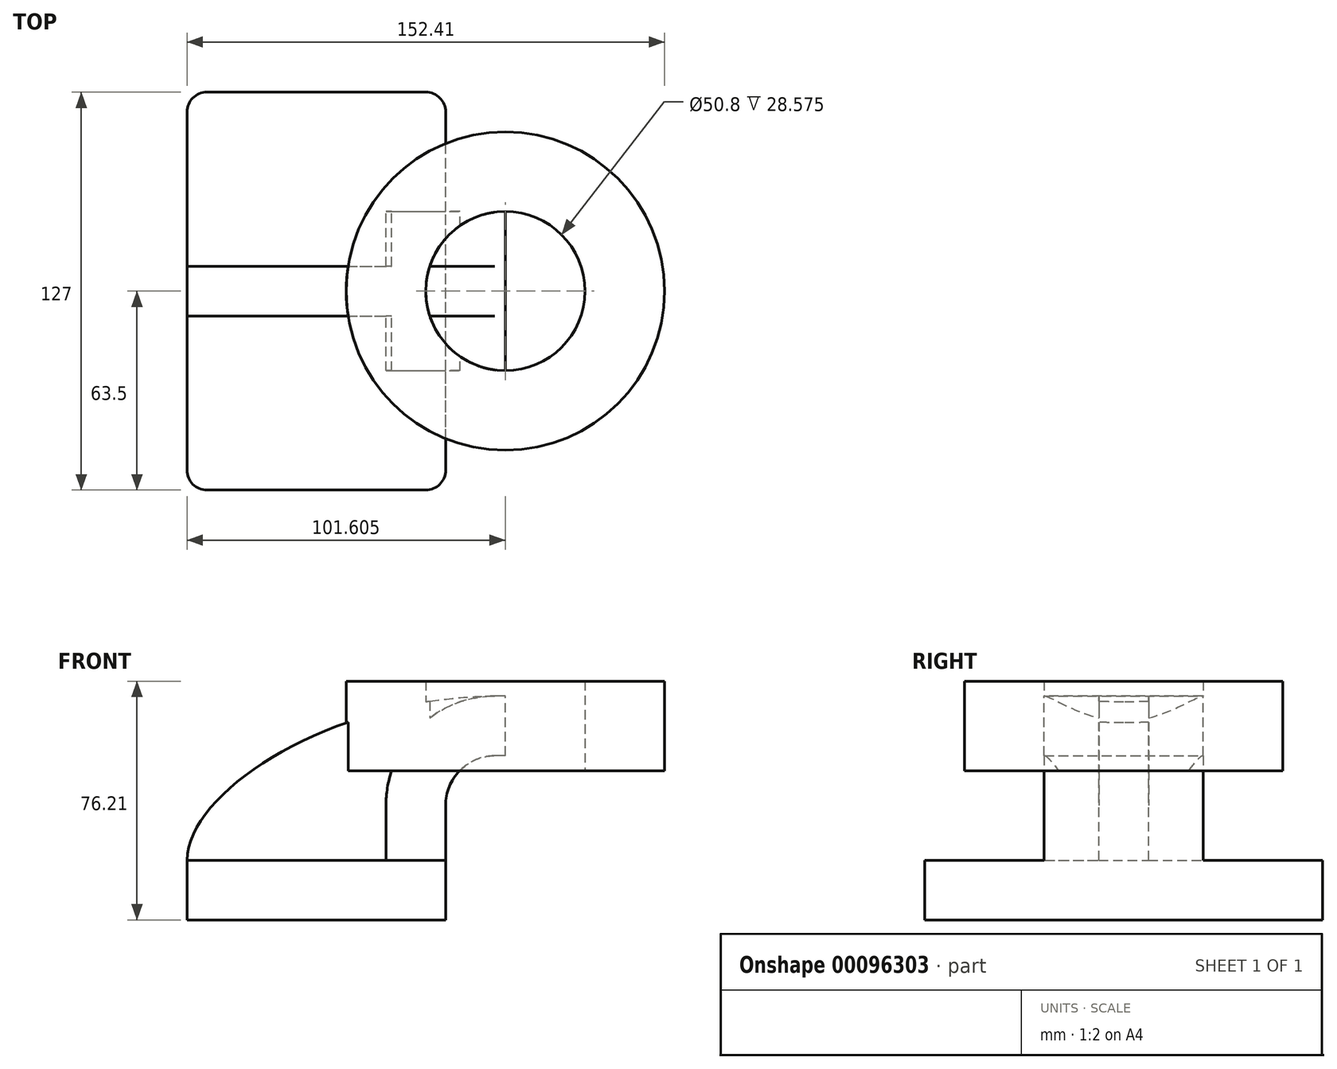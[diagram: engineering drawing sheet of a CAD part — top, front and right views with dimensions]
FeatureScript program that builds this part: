
annotation { "Feature Type Name" : "Feature", "Feature Type Description" : "" }
export const myFeature = defineFeature(function(context is Context, id is Id, definition is map)
    precondition{}
    {
        {
            var Q0;
            Q0=qCreatedBy(makeId("Front.planeOp"),FACE);
            var sketch = newSketch(context, id + "F0", { "sketchPlane" : qUnion([Q0])});
            skLineSegment(sketch, "E0.bottom", {"start": v(-41.28, -9.53) * mm, "end": v(41.28, -9.53) * mm});
            skLineSegment(sketch, "E0.top", {"start": v(-41.28, 9.53) * mm, "end": v(41.28, 9.53) * mm});
            skLineSegment(sketch, "E0.left", {"start": v(-41.28, -9.53) * mm, "end": v(-41.28, 9.53) * mm});
            skLineSegment(sketch, "E0.right", {"start": v(41.28, -9.53) * mm, "end": v(41.28, 9.53) * mm});
            skPoint(sketch, "E0.middle", {"position": v(0, 0) * mm});
            skLineSegment(sketch, "E1.bottom", {"start": v(60.33, 38.1) * mm, "end": v(111.12, 38.1) * mm});
            skLineSegment(sketch, "E1.top", {"start": v(60.33, 66.67) * mm, "end": v(111.12, 66.67) * mm});
            skLineSegment(sketch, "E1.left", {"start": v(60.33, 38.1) * mm, "end": v(60.33, 66.67) * mm});
            skLineSegment(sketch, "E1.right", {"start": v(111.12, 38.1) * mm, "end": v(111.12, 66.67) * mm});
            skPoint(sketch, "E1.middle", {"position": v(85.72, 52.39) * mm});
            skLineSegment(sketch, "E2", {"start": v(41.28, 9.53) * mm, "end": v(41.28, 27) * mm});
            skArc(sketch, "E3", {"start": v(41.27, 27) * mm, "mid": v(45.92, 38.23) * mm, "end": v(57.15, 42.88) * mm});
            skLineSegment(sketch, "E4", {"start": v(57.15, 42.88) * mm, "end": v(85.72, 42.88) * mm});
            skLineSegment(sketch, "E5.0", {"start": v(57.15, 61.93) * mm, "end": v(85.72, 61.93) * mm});
            skArc(sketch, "E5.1", {"start": v(22.23, 27) * mm, "mid": v(32.45, 51.7) * mm, "end": v(57.15, 61.93) * mm});
            skLineSegment(sketch, "E5.2", {"start": v(22.22, 9.53) * mm, "end": v(22.22, 27) * mm});
            skLineSegment(sketch, "E6", {"start": v(85.72, 38.1) * mm, "end": v(85.72, 66.67) * mm});
            skLineSegment(sketch, "E7", {"start": v(85.72, 66.67) * mm, "end": v(85.72, 38.1) * mm});
            skFitSpline(sketch, "E8", {"points": [v(-41.28, 9.53) * mm, v(57.15, 61.93) * mm], "startDerivative": vector(1.2, 70.15) * mm, "endDerivative": vector(147.8, 0.35) * mm});
            skSolve(sketch);
        }
        {
            var Q0;
            Q0=makeQuery(id+"F0.imprint","IMPRINT",FACE,{"disambiguationData":[TD([[makeQuery(id+"F0.imprint","IMPRINT",EDGE,{"derivedFrom":sQuery(id+"F0.wireOp",EDGE,"E0.bottom")}),1.0]])]});
            extrude(context, id + "F1", {"entities" : qUnion([Q0]), "endBound" : BoundingType.SYMMETRIC, "depth" : 127 * mm});
        }
        {
            var Q0;
            {var subQ1=sQuery(id+"F0.wireOp",EDGE,"E2");Q0=makeQuery(id+"F0.imprint","IMPRINT",FACE,{"disambiguationData":[TD([[makeQuery(id+"F0.imprint","IMPRINT",EDGE,{"derivedFrom":subQ1}),1.0]])]});}
            extrude(context, id + "F2", {"entities" : qUnion([Q0]), "operationType" : NewBodyOperationType.ADD, "endBound" : BoundingType.SYMMETRIC, "depth" : 50.8 * mm});
        }
        {
            var Q0;
            {var subQ3=sQuery(id+"F0.wireOp",EDGE,"E5.2");Q0=makeQuery(id+"F0.imprint","IMPRINT",FACE,{"disambiguationData":[TD([[makeQuery(id+"F0.imprint","IMPRINT",EDGE,{"derivedFrom":subQ3}),1.0]])]});}
            extrude(context, id + "F3", {"entities" : qUnion([Q0]), "operationType" : NewBodyOperationType.ADD, "endBound" : BoundingType.SYMMETRIC, "depth" : 15.88 * mm});
        }
        {
            var Q0;
            {var subQ0=sQuery(id+"F0.wireOp",EDGE,"E1.right");Q0=makeQuery(id+"F0.imprint","IMPRINT",FACE,{"disambiguationData":[TD([[makeQuery(id+"F0.imprint","IMPRINT",EDGE,{"derivedFrom":subQ0}),1.0]])]});}
            var Q1;
            Q1=sQuery(id+"F0.wireOp",EDGE,"E1.left");
            revolve(context, id + "F4", {"operationType" : NewBodyOperationType.ADD, "entities" : qUnion([Q0]), "axis" : qUnion([Q1]), "revolveType" : RevolveType.FULL});
        }
        {
            var Q0;
            Q0=makeQuery(id+"F1.opExtrude","CAP_EDGE",EDGE,{"disambiguationData":[OSD([sQuery(id+"F0.wireOp",EDGE,"E0.right")])],"isStart":false});
            var Q1;
            Q1=makeQuery(id+"F1.opExtrude","CAP_EDGE",EDGE,{"disambiguationData":[OSD([sQuery(id+"F0.wireOp",EDGE,"E0.left")])],"isStart":false});
            var Q2;
            Q2=makeQuery(id+"F1.opExtrude","CAP_EDGE",EDGE,{"disambiguationData":[OSD([sQuery(id+"F0.wireOp",EDGE,"E0.left")])],"isStart":true});
            var Q3;
            Q3=makeQuery(id+"F1.opExtrude","CAP_EDGE",EDGE,{"disambiguationData":[OSD([sQuery(id+"F0.wireOp",EDGE,"E0.right")])],"isStart":true});
            fillet(context, id + "F5", {"entities" : qUnion([Q0, Q1, Q2, Q3]), "radius" : 6.35 * mm, "tangentPropagation" : true, "allowEdgeOverflow" : false});
        }
    });
